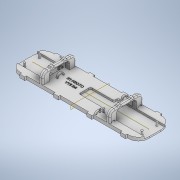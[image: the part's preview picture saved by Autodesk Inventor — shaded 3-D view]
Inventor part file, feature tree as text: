
AUTODESK INVENTOR PART (.ipt)
format: ipt  version: 2021 (Build 250183000, 183)  size: 2,459,648 bytes
history: native  units: in
note: dims shown in document units (in); Inventor stores cm internally (conversion verified against a paired STEP export)
features: sketch x11, extrude x10, mirror x7, fillet x6, plane x2, revolve x2
ambient origin geometry x8: Origin, YZ Plane, XZ Plane, XY Plane, X Axis, Y Axis, Z Axis, Center Point
bodies: Solid1 (feature_tree)
feature tree (38):
  extrude  "Extrusion1"  Depth=4.9606in
  extrude  "Extrusion2"  TaperAngle=0.0deg  [1 undecoded]
  plane  "Work Plane1"
  plane  "Work Plane2"
  extrude  "Extrusion5"  Depth=0.0787in
  fillet  "Fillet2"  Radius=0.0787in
  mirror  "Mirror3"
  extrude  "Extrusion6"  TaperAngle=0.0deg  [1 undecoded]
  extrude  "Extrusion7"  Depth=0.2362in
  extrude  "Extrusion9"  [1 undecoded]
  extrude  "Extrusion10"  Depth=0.5354in
  fillet  "Fillet4"  Radius=0.9449in
  mirror  "Mirror4"
  mirror  "Mirror5"
  fillet  "Fillet5"  Radius=2.7559in
  extrude  "Extrusion11"  Depth=0.811in
  fillet  "Fillet6"  Radius=0.0866in
  extrude  "Extrusion12"  Depth=0.0945in
  revolve  "Revolution5"  [1 undecoded]
  extrude  "Extrusion13"  TaperAngle=0.0deg  [1 undecoded]
  mirror  "Mirror8"
  mirror  "Mirror9"
  mirror  "Mirror10"
  fillet  "Fillet9"  [1 undecoded]
  fillet  "Fillet11"  [1 undecoded]
  revolve  "Revolution6"  [1 undecoded]
  mirror  "Mirror11"
  sketch  "Sketch1"  dims[d0=0.1575in d1=0.0in d2=4.9606in]
  sketch  "Sketch2"  dims[d3=1.5512in d4=0.0in]
  sketch  "Sketch7"  dims[d5=0.0in d6=0.2362in d7=0.0787in d8=0.0in]
  sketch  "Sketch8"  dims[d15=-0.7756in d16=0.0in]
  sketch  "Sketch13"  dims[d17=0.0in d18=0.2362in]
  sketch  "Sketch14"  dims[d19=1.3386in d24=-2.4803in]
  sketch  "Sketch15"  dims[d28=0.5354in d29=0.0in d30=0.5354in d31=0.9449in d32=2.7559in]
  sketch  "Sketch25"  dims[d33=0.4724in d34=0.811in d35=0.0866in d36=0.0in]
  sketch  "Sketch26"  dims[d37=0.0945in d38=0.0945in]
  sketch  "Sketch27"  dims[d39=0.0945in d40=0.0945in]
  sketch  "Sketch31"  dims[d41=0.0in d42=0.0in d43=0.0in d44=0.0in d45=0.7in d46=1.8in d47=0.35in d48=0.1575in d49=0.0in d60=1.9685in d61=0.9449in d62=0.4724in d63=1.7087in d64=0.0945in d65=0.0945in d66=0.0945in d67=0.0945in d68=0.0in d69=0.0in d70=0.0in d71=0.0in d72=0.9in d73=0.7in d74=0.35in d75=0.1969in d79=0.4094in d80=0.0in d81=0.0in d82=0.0in d83=0.0in d84=0.0in d85=0.0787in d86=0.0in d88=0.2362in d89=0.1575in d90=0.7874in d91=0.3937in d92=0.0394in d93=0.0in d96=1.1024in d97=0.5512in d98=0.2756in d99=0.0787in d116=0.2362in d117=0.0in d118=0.0in d119=0.1181in d120=0.0394in d121=0.0in d122=0.0787in d123=0.0472in d124=180.0deg d125=0.1181in d126=0.1575in d127=0.0157in d128=0.0in d131=0.0394in d133=0.0551in d134=0.0in d138=0.5709in d139=0.0787in d140=0.0394in d141=0.3031in d142=0.1516in d143=180.0deg d144=0.0394in d146=0.0197in d147=0.0344in d148=0.0197in d149=0.0344in]
note: 8 required parameter values undecoded (feature->parameter linkage not recoverable at this tier; creation-order binding heuristic only, values carry confidence <= 0.55)